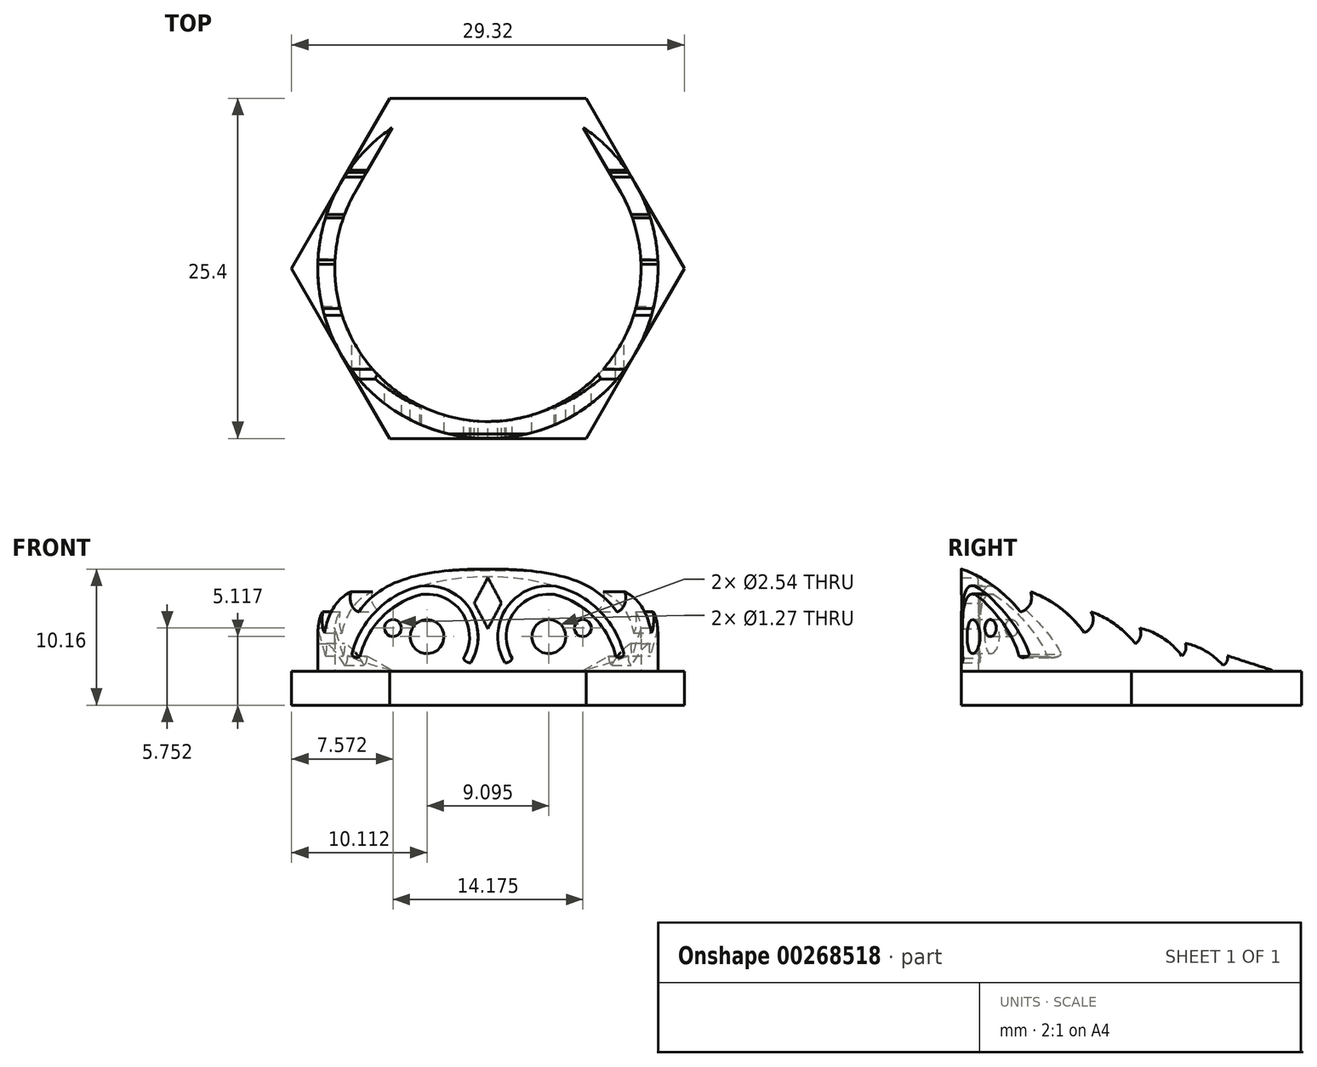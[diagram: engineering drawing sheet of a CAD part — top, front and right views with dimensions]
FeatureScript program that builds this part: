
annotation { "Feature Type Name" : "Feature", "Feature Type Description" : "" }
export const myFeature = defineFeature(function(context is Context, id is Id, definition is map)
    precondition{}
    {
        {
            var Q0;
            Q0=qCreatedBy(makeId("Top.planeOp"),FACE);
            var sketch = newSketch(context, id + "F0", { "sketchPlane" : qUnion([Q0])});
            skArc(sketch, "E0", {"start": v(-9.9, 5.71) * mm, "mid": v(0, -11.43) * mm, "end": v(9.9, 5.71) * mm});
            skArc(sketch, "E1", {"start": v(-7.13, 10.5) * mm, "mid": v(0, -12.7) * mm, "end": v(7.13, 10.5) * mm});
            skLineSegment(sketch, "E2", {"start": v(-9.9, 5.72) * mm, "end": v(-7.13, 10.5) * mm});
            skLineSegment(sketch, "E3", {"start": v(7.13, 10.5) * mm, "end": v(9.9, 5.71) * mm});
            skLineSegment(sketch, "E4", {"start": v(0, 0) * mm, "end": v(9.9, 5.71) * mm, "construction": true});
            skLineSegment(sketch, "E5", {"start": v(0, 0) * mm, "end": v(-9.9, 5.72) * mm, "construction": true});
            skSolve(sketch);
        }
        {
            var Q0;
            Q0 = qSketchRegion(id + "F0", true);
            extrude(context, id + "F1", {"entities" : qUnion([Q0]), "depth" : 7.62 * mm});
        }
        {
            var Q0;
            Q0=qCreatedBy(makeId("Right.planeOp"),FACE);
            var sketch = newSketch(context, id + "F2", { "sketchPlane" : qUnion([Q0])});
            skLineSegment(sketch, "E6", {"start": v(10.67, 0.02) * mm, "end": v(-12.7, 7.62) * mm});
            skLineSegment(sketch, "E7", {"start": v(10.67, 0.02) * mm, "end": v(10.67, 7.64) * mm});
            skLineSegment(sketch, "E8", {"start": v(10.67, 7.64) * mm, "end": v(-12.7, 7.62) * mm});
            skPoint(sketch, "E9.end.orphan", {"position": v(-12.43, 0.02) * mm});
            skSolve(sketch);
        }
        {
            var Q0;
            Q0 = qSketchRegion(id + "F2", true);
            extrude(context, id + "F3", {"entities" : qUnion([Q0]), "operationType" : NewBodyOperationType.REMOVE, "endBound" : BoundingType.SYMMETRIC, "oppositeDirection" : true, "depth" : 50.8 * mm});
        }
        {
            var Q0;
            Q0=qCreatedBy(makeId("Front.planeOp"),FACE);
            var sketch = newSketch(context, id + "F4", { "sketchPlane" : qUnion([Q0])});
            skLineSegment(sketch, "E10", {"start": v(0, 0) * mm, "end": v(0, 9.53) * mm, "construction": true});
            skArc(sketch, "E11", {"start": v(-1.27, 0.63) * mm, "mid": v(-1.38, 4.7) * mm, "end": v(-5.08, 6.35) * mm});
            skArc(sketch, "E12", {"start": v(-5.08, 6.35) * mm, "mid": v(-8.32, 4.51) * mm, "end": v(-10.16, 1.27) * mm});
            skArc(sketch, "E13.0", {"start": v(-4.96, 5.73) * mm, "mid": v(-7.89, 4.05) * mm, "end": v(-9.54, 1.12) * mm});
            skArc(sketch, "E13.1", {"start": v(-1.82, 0.96) * mm, "mid": v(-1.9, 4.32) * mm, "end": v(-4.96, 5.73) * mm});
            skArc(sketch, "E14", {"start": v(-10.16, 1.27) * mm, "mid": v(-9.9, 1.03) * mm, "end": v(-9.54, 1.12) * mm});
            skArc(sketch, "E15", {"start": v(-1.82, 0.96) * mm, "mid": v(-1.6, 0.7) * mm, "end": v(-1.27, 0.63) * mm});
            skCircle(sketch, "E16", {"center": v(-4.55, 2.58) * mm, "radius": 1.27 * mm});
            skCircle(sketch, "E17", {"center": v(-7.09, 3.21) * mm, "radius": 0.64 * mm});
            skLineSegment(sketch, "E18", {"start": v(0, 3.17) * mm, "end": v(-1.02, 5.08) * mm});
            skLineSegment(sketch, "E19", {"start": v(-1.02, 5.08) * mm, "end": v(0, 6.99) * mm});
            skLineSegment(sketch, "E20.MirrorCS", {"start": v(1.02, 5.08) * mm, "end": v(0, 6.99) * mm});
            skLineSegment(sketch, "E21.MirrorCS", {"start": v(0, 3.17) * mm, "end": v(1.02, 5.08) * mm});
            skArc(sketch, "E22.MirrorCS", {"start": v(1.27, 0.63) * mm, "mid": v(1.38, 4.7) * mm, "end": v(5.08, 6.35) * mm});
            skArc(sketch, "E23.MirrorCS", {"start": v(1.82, 0.96) * mm, "mid": v(1.9, 4.32) * mm, "end": v(4.96, 5.73) * mm});
            skArc(sketch, "E24.MirrorCS", {"start": v(1.82, 0.96) * mm, "mid": v(1.6, 0.7) * mm, "end": v(1.27, 0.63) * mm});
            skArc(sketch, "E25.MirrorCS", {"start": v(5.08, 6.35) * mm, "mid": v(8.32, 4.51) * mm, "end": v(10.16, 1.27) * mm});
            skArc(sketch, "E26.MirrorCS", {"start": v(4.96, 5.73) * mm, "mid": v(7.89, 4.05) * mm, "end": v(9.54, 1.12) * mm});
            skCircle(sketch, "E27.MirrorC", {"center": v(7.09, 3.21) * mm, "radius": 0.64 * mm});
            skCircle(sketch, "E28.MirrorC", {"center": v(4.55, 2.58) * mm, "radius": 1.27 * mm});
            skArc(sketch, "E29.MirrorCS", {"start": v(10.16, 1.27) * mm, "mid": v(9.9, 1.03) * mm, "end": v(9.54, 1.12) * mm});
            skSolve(sketch);
        }
        {
            var Q0;
            Q0 = qSketchRegion(id + "F4", true);
            extrude(context, id + "F5", {"entities" : qUnion([Q0]), "operationType" : NewBodyOperationType.REMOVE, "depth" : 25.4 * mm});
        }
        {
            var Q0;
            Q0=qCreatedBy(makeId("Right.planeOp"),FACE);
            var sketch = newSketch(context, id + "F6", { "sketchPlane" : qUnion([Q0])});
            skArc(sketch, "E30", {"start": v(-8.28, 4.42) * mm, "mid": v(-10.28, 6.34) * mm, "end": v(-12.72, 7.65) * mm});
            skArc(sketch, "E31", {"start": v(-8.28, 4.42) * mm, "mid": v(-7.55, 5) * mm, "end": v(-7.53, 5.93) * mm});
            skArc(sketch, "E32", {"start": v(-3.52, 2.86) * mm, "mid": v(-5.3, 4.7) * mm, "end": v(-7.53, 5.93) * mm});
            skArc(sketch, "E33", {"start": v(-3.52, 2.86) * mm, "mid": v(-2.9, 3.53) * mm, "end": v(-3.01, 4.42) * mm});
            skArc(sketch, "E34", {"start": v(0.3, 2.05) * mm, "mid": v(-1.2, 3.48) * mm, "end": v(-3.01, 4.42) * mm});
            skArc(sketch, "E35", {"start": v(0.3, 2.05) * mm, "mid": v(0.68, 2.57) * mm, "end": v(0.63, 3.22) * mm});
            skArc(sketch, "E36", {"start": v(3.76, 1.14) * mm, "mid": v(2.38, 2.46) * mm, "end": v(0.63, 3.22) * mm});
            skArc(sketch, "E37", {"start": v(3.76, 1.14) * mm, "mid": v(4.06, 1.57) * mm, "end": v(4.01, 2.1) * mm});
            skArc(sketch, "E38", {"start": v(6.82, 0.44) * mm, "mid": v(7.13, 0.72) * mm, "end": v(7.16, 1.14) * mm});
            skLineSegment(sketch, "E39", {"start": v(-12.72, 7.65) * mm, "end": v(4.18, 2.12) * mm});
            skLineSegment(sketch, "E40.trimOffspring", {"start": v(5.1, 1.82) * mm, "end": v(7.16, 1.14) * mm});
            skLineSegment(sketch, "E41", {"start": v(4.18, 2.12) * mm, "end": v(5.1, 1.82) * mm});
            skArc(sketch, "E42", {"start": v(6.82, 0.44) * mm, "mid": v(5.54, 1.5) * mm, "end": v(4, 2.1) * mm});
            skLineSegment(sketch, "E43", {"start": v(-12.72, 7.65) * mm, "end": v(-12.35, 8.76) * mm});
            skLineSegment(sketch, "E44", {"start": v(-12.35, 8.76) * mm, "end": v(12.27, 0) * mm});
            skLineSegment(sketch, "E45", {"start": v(12.27, 0) * mm, "end": v(7.16, 1.14) * mm});
            skSolve(sketch);
        }
        {
            var Q0;
            Q0 = qSketchRegion(id + "F6", true);
            extrude(context, id + "F7", {"entities" : qUnion([Q0]), "operationType" : NewBodyOperationType.REMOVE, "endBound" : BoundingType.SYMMETRIC, "oppositeDirection" : true, "depth" : 508 * mm});
        }
        {
            var Q0;
            Q0=makeQuery(id+"F1.opExtrude","CAP_FACE",FACE,{"disambiguationData":[OSD([sQuery(id+"F0.wireOp",EDGE,"E0"),sQuery(id+"F0.wireOp",EDGE,"E1"),sQuery(id+"F0.wireOp",EDGE,"E2"),sQuery(id+"F0.wireOp",EDGE,"E3")])],"isStart":true});
            var sketch = newSketch(context, id + "F8", { "sketchPlane" : qUnion([Q0])});
            skCircle(sketch, "E46.cCircle", {"center": v(0, 0) * mm, "radius": 12.7 * mm, "construction": true});
            skLineSegment(sketch, "E46.0", {"start": v(7.33, 12.7) * mm, "end": v(14.66, 0) * mm});
            skLineSegment(sketch, "E46.1", {"start": v(14.66, 0) * mm, "end": v(7.33, -12.7) * mm});
            skLineSegment(sketch, "E46.2", {"start": v(7.33, -12.7) * mm, "end": v(-7.33, -12.7) * mm});
            skLineSegment(sketch, "E46.3", {"start": v(-7.33, -12.7) * mm, "end": v(-14.66, 0) * mm});
            skLineSegment(sketch, "E46.4", {"start": v(-14.66, 0) * mm, "end": v(-7.33, 12.7) * mm});
            skLineSegment(sketch, "E46.5", {"start": v(-7.33, 12.7) * mm, "end": v(7.33, 12.7) * mm});
            skPoint(sketch, "E46.0.midPoint", {"position": v(11, 6.35) * mm});
            skSolve(sketch);
        }
        {
            var Q0;
            Q0 = qSketchRegion(id + "F8", true);
            extrude(context, id + "F9", {"entities" : qUnion([Q0]), "operationType" : NewBodyOperationType.ADD, "depth" : 2.54 * mm});
        }
    });
